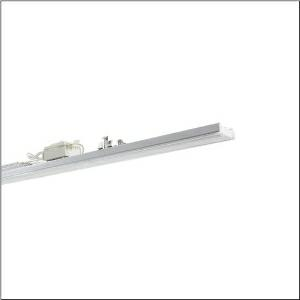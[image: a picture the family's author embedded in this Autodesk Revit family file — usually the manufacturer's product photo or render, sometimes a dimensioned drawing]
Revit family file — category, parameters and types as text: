
# Revit family: licross_21_recessed_ho_52te12dn4fxm3c
name_source: partatom
category: Lighting Fixtures
units: mm (PartAtom-declared; Revit-internal decimal feet)

## family parameters
Cut with Voids When Loaded = No
Host = Face
Light Source = No
Part Type = Normal
Room Calculation Point = No
Round Connector Dimension = Use Diameter
Shared = No

## types (1)
- --- (1 x LED, 930 lm, 7.5 W, 4000K)
    Apparent Load = 8 VA
    CIE Flux Codes = 69 91 98 100 100
    Color Rendering = 80
    Color Temperature = 4000K
    Default Elevation = 1800 mm
    Description = Licross 21 Recessed HO, luminaire insert, of sheet steel, galvanised, coil coated, white, length: 1.500mm, width: 66mm, height: 67mm, LED rated luminous flux: 15.000lm, light colour: 840, SDCM (Standard Deviation of Colour Matching)MacAdam ≤ 3 SDCM (initial), control gear: DALI 2 (for two DALI lines), with plug, 6-pole, with phase selection, for trunking rail, 14-core, mains connection: 220..240V, AC, 50/60Hz, rated input power: 88W, internal wiring halogen-free, for emergency light function, for trunking rail, 14-core, converter,control gear: single battery element, battery: LiFePO4, 9Ah, primary optical cover: cover, of PMMA, light emission: direct distribution, primary light characteristic: symmetric, protection rating (complete): IP54, insulation class (complete): insulation class I (protective earthing), certification: CE, UKCA, protection symbol: D if used in an environment with non-conductive dust loads with corresponding accessories, impact resistance: IK06, permissible ambient temperature for indoor applications: +5..+30°C, standard: EN 60598-2-22, LABS conformity tested according to VDMA 24364:2018-05, reducing of maximum allowable ambient temperature of 5°C with ceiling mounting, corresponds to IFS (International Featured Standards) requirements for safety and quality in the food industry, The light source and the operating device comply with the requirements of the Ecodesign Regulation (EU) 2019/2020 and are replaceable in accordance with this regulation, packaging unit: 1 piece
    Height = 58 mm
    Lamp = 1 x LED
    Lamp Light Flux = 930 lm
    Lamp Power = 7.5 W
    Lamp count = 1
    Length = 1500 mm
    Luminous efficacy = 124 lm/W
    Manufacturer = Siteco
    ModVariant = No
    Model = 52TE12DN4FXM3C
    Mounting Place = Ceiling
    Mounting Type = Pendant
    Number of Poles = 1
    OnlyDefault = Yes
    Power Factor = 1
    Product Name = Licross 21 Recessed HO
    Product group = luminaire insert | ceiling pendant
    ProductGroupID = 901
    Protection Class = Protection class I
    Protection Degree = IP 54
    RLX_Detail_Level = 1
    RLX_Emergency_Light_Flux = 0 lm
    RLX_Emergency_Type = 0
    RLX_Emergency_Type_DB = No
    RlxData = <blob elided: 25473 chars, md5=185efb52>
    Socket = socket
    Standby Power = 0 W
    System Light Flux = 930 lm
    System Power = 8 W
    Type Comments = : emergency light operation: 3 h
    Type Image = l_1296930.jpg
    URL = http://relux.com
    VarID = @adj_109221
    Voltage = 0 V
    Weight = 0.00 kg
    Width = 66 mm

## geometry (parser evidence)
native form markers: Blend x4, Sweep x9
no freeform markers — native parametric forms only
